FCSTD DOCUMENT  (FreeCAD 0.19R24276 (Git))
Label: Master_sketch_3_1
License: All rights reserved
LicenseURL: http://en.wikipedia.org/wiki/All_rights_reserved
objects: Sketcher::SketchObject×1, PartDesign::Body×1
note: 2 computed .brp shape members not serialized (recipe doc carries the construction recipe); baked Part::Feature solids carry a one-line shape summary decoded from their .brp

FEATURE [Sketcher::SketchObject] Sketch
  FullyConstrained = false
  MapMode = 5
  Support = -> [XY_Plane]
  sketch-geometry (179):
    g0: LineSegment StartX=-41 StartY=82 StartZ=0 EndX=39 EndY=82 EndZ=0
    g1: LineSegment StartX=39 StartY=82 StartZ=0 EndX=39 EndY=71 EndZ=0
    g2: LineSegment StartX=39 StartY=71 StartZ=0 EndX=-41 EndY=71 EndZ=0
    g3: LineSegment StartX=-41 StartY=71 StartZ=0 EndX=-41 EndY=82 EndZ=0
    g4: LineSegment StartX=-26 StartY=82 StartZ=0 EndX=-26 EndY=71 EndZ=0
    g5: LineSegment StartX=24 StartY=82 StartZ=0 EndX=24 EndY=71 EndZ=0
    g6: LineSegment StartX=-41 StartY=71 StartZ=0 EndX=-26 EndY=82 EndZ=0
    g7: LineSegment StartX=-41 StartY=82 StartZ=0 EndX=-26 EndY=71 EndZ=0
    g8: LineSegment StartX=24 StartY=71 StartZ=0 EndX=39 EndY=82 EndZ=0
    g9: LineSegment StartX=24 StartY=82 StartZ=0 EndX=39 EndY=71 EndZ=0
    g10: LineSegment StartX=-41 StartY=108 StartZ=0 EndX=39 EndY=108 EndZ=0
    g11: LineSegment StartX=39 StartY=108 StartZ=0 EndX=39 EndY=119 EndZ=0
    g12: LineSegment StartX=39 StartY=119 StartZ=0 EndX=-41 EndY=119 EndZ=0
    g13: LineSegment StartX=-41 StartY=119 StartZ=0 EndX=-41 EndY=108 EndZ=0
    g14: LineSegment StartX=-26 StartY=108 StartZ=0 EndX=-26 EndY=119 EndZ=0
    g15: LineSegment StartX=24 StartY=108 StartZ=0 EndX=24 EndY=119 EndZ=0
    g16: LineSegment StartX=-41 StartY=119 StartZ=0 EndX=-26 EndY=108 EndZ=0
    g17: LineSegment StartX=-41 StartY=108 StartZ=0 EndX=-26 EndY=119 EndZ=0
    g18: LineSegment StartX=24 StartY=119 StartZ=0 EndX=39 EndY=108 EndZ=0
    g19: LineSegment StartX=24 StartY=108 StartZ=0 EndX=39 EndY=119 EndZ=0
    g20: LineSegment StartX=-41 StartY=153 StartZ=0 EndX=14 EndY=153 EndZ=0
    g21: LineSegment StartX=39 StartY=153 StartZ=0 EndX=39 EndY=142 EndZ=0
    g22: LineSegment StartX=39 StartY=142 StartZ=0 EndX=19 EndY=142 EndZ=0
    g23: LineSegment StartX=-41 StartY=142 StartZ=0 EndX=-41 EndY=153 EndZ=0
    g24: LineSegment StartX=-26 StartY=153 StartZ=0 EndX=-26 EndY=142 EndZ=0
    g25: LineSegment StartX=24 StartY=153 StartZ=0 EndX=24 EndY=142 EndZ=0
    g26: LineSegment StartX=-41 StartY=142 StartZ=0 EndX=-26 EndY=153 EndZ=0
    g27: LineSegment StartX=-41 StartY=153 StartZ=0 EndX=-26 EndY=142 EndZ=0
    g28: LineSegment StartX=24 StartY=142 StartZ=0 EndX=39 EndY=153 EndZ=0
    g29: LineSegment StartX=24 StartY=153 StartZ=0 EndX=39 EndY=142 EndZ=0
    g30: LineSegment StartX=-116.97 StartY=98 StartZ=0 EndX=24 EndY=98 EndZ=0
    g31: LineSegment StartX=24 StartY=98 StartZ=0 EndX=24 EndY=92 EndZ=0
    g32: LineSegment StartX=24 StartY=92 StartZ=0 EndX=-116.97 EndY=92 EndZ=0
    g33: LineSegment StartX=-116.97 StartY=92 StartZ=0 EndX=-116.97 EndY=98 EndZ=0
    g34: LineSegment StartX=-25 StartY=122 StartZ=0 EndX=-12.5 EndY=122 EndZ=0
    g35: LineSegment StartX=23 StartY=122 StartZ=0 EndX=23 EndY=70 EndZ=0
    g36: LineSegment StartX=23 StartY=70 StartZ=0 EndX=-25 EndY=70 EndZ=0
    g37: LineSegment StartX=12.5 StartY=122 StartZ=0 EndX=12.5 EndY=201.661 EndZ=0
    g38: LineSegment StartX=12.5 StartY=201.661 StartZ=0 EndX=-12.5 EndY=201.661 EndZ=0
    g39: LineSegment StartX=-12.5 StartY=201.661 StartZ=0 EndX=-12.5 EndY=122 EndZ=0
    g40: LineSegment StartX=19 StartY=153 StartZ=0 EndX=19 EndY=142 EndZ=0
    g41: LineSegment StartX=14 StartY=131 StartZ=0 EndX=14 EndY=153 EndZ=0
    g42: LineSegment StartX=14 StartY=131 StartZ=0 EndX=43.35 EndY=131 EndZ=0
    g43: LineSegment StartX=60.35 StartY=140 StartZ=0 EndX=24 EndY=140 EndZ=0
    g44: LineSegment StartX=60.35 StartY=140 StartZ=0 EndX=60.35 EndY=10 EndZ=0
    g45: LineSegment StartX=43.35 StartY=70 StartZ=0 EndX=43.35 EndY=102 EndZ=0
    g46: LineSegment StartX=25.35 StartY=70 StartZ=0 EndX=43.35 EndY=70 EndZ=0
    g47: LineSegment StartX=25.35 StartY=107 StartZ=0 EndX=43.35 EndY=107 EndZ=0
    g48: LineSegment StartX=43.35 StartY=102 StartZ=0 EndX=25.35 EndY=102 EndZ=0
    g49: LineSegment StartX=25.35 StartY=102 StartZ=0 EndX=25.35 EndY=107 EndZ=0
    g50: LineSegment StartX=43.35 StartY=107 StartZ=0 EndX=43.35 EndY=131 EndZ=0
    g51: LineSegment StartX=14 StartY=142 StartZ=0 EndX=-41 EndY=142 EndZ=0
    g52: LineSegment StartX=-115.97 StartY=100 StartZ=0 EndX=-99.97 EndY=100 EndZ=0
    g53: LineSegment StartX=-99.97 StartY=100 StartZ=0 EndX=-99.97 EndY=90 EndZ=0
    g54: LineSegment StartX=-99.97 StartY=90 StartZ=0 EndX=-115.97 EndY=90 EndZ=0
    g55: LineSegment StartX=-115.97 StartY=90 StartZ=0 EndX=-115.97 EndY=100 EndZ=0
    g56: LineSegment StartX=-110.97 StartY=90 StartZ=0 EndX=-104.97 EndY=90 EndZ=0
    g57: LineSegment StartX=-104.97 StartY=90 StartZ=0 EndX=-104.97 EndY=80 EndZ=0
    g58: LineSegment StartX=-104.97 StartY=80 StartZ=0 EndX=-110.97 EndY=80 EndZ=0
    g59: LineSegment StartX=-110.97 StartY=80 StartZ=0 EndX=-110.97 EndY=90 EndZ=0
    g60: LineSegment StartX=-123.97 StartY=80 StartZ=0 EndX=-91.97 EndY=80 EndZ=0
    g61: LineSegment StartX=-91.97 StartY=80 StartZ=0 EndX=-91.97 EndY=30 EndZ=0
    g62: LineSegment StartX=-91.97 StartY=30 StartZ=0 EndX=-123.97 EndY=30 EndZ=0
    g63: LineSegment StartX=-123.97 StartY=30 StartZ=0 EndX=-123.97 EndY=80 EndZ=0
    g64: LineSegment StartX=-41 StartY=193.983 StartZ=0 EndX=14 EndY=193.983 EndZ=0
    g65: LineSegment StartX=39 StartY=193.983 StartZ=0 EndX=39 EndY=182.983 EndZ=0
    g66: LineSegment StartX=39 StartY=182.983 StartZ=0 EndX=19 EndY=182.983 EndZ=0
    g67: LineSegment StartX=-41 StartY=182.983 StartZ=0 EndX=-41 EndY=193.983 EndZ=0
    g68: LineSegment StartX=-26 StartY=193.983 StartZ=0 EndX=-26 EndY=182.983 EndZ=0
    g69: LineSegment StartX=24 StartY=193.983 StartZ=0 EndX=24 EndY=182.983 EndZ=0
    g70: LineSegment StartX=-41 StartY=182.983 StartZ=0 EndX=-26 EndY=193.983 EndZ=0
    g71: LineSegment StartX=-41 StartY=193.983 StartZ=0 EndX=-26 EndY=182.983 EndZ=0
    g72: LineSegment StartX=24 StartY=182.983 StartZ=0 EndX=39 EndY=193.983 EndZ=0
    g73: LineSegment StartX=24 StartY=193.983 StartZ=0 EndX=39 EndY=182.983 EndZ=0
    g74: LineSegment StartX=-26 StartY=142 StartZ=0 EndX=55.8269 EndY=142 EndZ=0
    g75: LineSegment StartX=55.8269 StartY=142 StartZ=0 EndX=55.8269 EndY=181.174 EndZ=0
    g76: LineSegment StartX=55.8269 StartY=181.174 StartZ=0 EndX=-36.273 EndY=181.174 EndZ=0
    g77: LineSegment StartX=-26 StartY=156.804 StartZ=0 EndX=-26 EndY=142 EndZ=0
    g78: LineSegment StartX=24 StartY=142 StartZ=0 EndX=-57.8269 EndY=142 EndZ=0
    g79: LineSegment StartX=-57.8269 StartY=142 StartZ=0 EndX=-57.8269 EndY=155.698 EndZ=0
    g80: LineSegment StartX=-57.8269 StartY=155.698 StartZ=0 EndX=34.273 EndY=155.698 EndZ=0
    g81: LineSegment StartX=24 StartY=157.131 StartZ=0 EndX=24 EndY=142 EndZ=0
    g82: LineSegment StartX=64.4469 StartY=144 StartZ=0 EndX=-180 EndY=144 EndZ=0
    g83: LineSegment StartX=-180 StartY=150 StartZ=0 EndX=64.4469 EndY=150 EndZ=0
    g84: LineSegment StartX=64.4469 StartY=150 StartZ=0 EndX=64.4469 EndY=144 EndZ=0
    g85: LineSegment StartX=24 StartY=142 StartZ=0 EndX=24 EndY=140 EndZ=0
    g86: LineSegment StartX=25.35 StartY=70 StartZ=0 EndX=25.35 EndY=10 EndZ=0
    g87: LineSegment StartX=25.35 StartY=10 StartZ=0 EndX=60.35 EndY=10 EndZ=0
    g88: LineSegment StartX=-27.35 StartY=70 StartZ=0 EndX=-62.35 EndY=70 EndZ=0
    g89: LineSegment StartX=-62.35 StartY=70 StartZ=0 EndX=-62.35 EndY=10 EndZ=0
    g90: LineSegment StartX=-62.35 StartY=10 StartZ=0 EndX=-27.35 EndY=10 EndZ=0
    g91: LineSegment StartX=-27.35 StartY=10 StartZ=0 EndX=-27.35 EndY=70 EndZ=0
    g92: LineSegment StartX=60.35 StartY=10 StartZ=0 EndX=-239.65 EndY=10 EndZ=0
    g93: LineSegment StartX=-239.65 StartY=10 StartZ=0 EndX=-239.65 EndY=0 EndZ=0
    g94: LineSegment StartX=-239.65 StartY=0 StartZ=0 EndX=60.35 EndY=0 EndZ=0
    g95: LineSegment StartX=60.35 StartY=0 StartZ=0 EndX=60.35 EndY=10 EndZ=0
    g96: LineSegment StartX=110 StartY=202.513 StartZ=0 EndX=190 EndY=202.513 EndZ=0
    g97: LineSegment StartX=190 StartY=202.513 StartZ=0 EndX=190 EndY=213.513 EndZ=0
    g98: LineSegment StartX=190 StartY=213.513 StartZ=0 EndX=110 EndY=213.513 EndZ=0
    g99: LineSegment StartX=110 StartY=213.513 StartZ=0 EndX=110 EndY=202.513 EndZ=0
    g100: LineSegment StartX=125 StartY=202.513 StartZ=0 EndX=125 EndY=213.513 EndZ=0
    g101: LineSegment StartX=175 StartY=202.513 StartZ=0 EndX=175 EndY=213.513 EndZ=0
    g102: LineSegment StartX=110 StartY=213.513 StartZ=0 EndX=125 EndY=202.513 EndZ=0
    g103: LineSegment StartX=110 StartY=202.513 StartZ=0 EndX=125 EndY=213.513 EndZ=0
    g104: LineSegment StartX=175 StartY=213.513 StartZ=0 EndX=190 EndY=202.513 EndZ=0
    g105: LineSegment StartX=175 StartY=202.513 StartZ=0 EndX=190 EndY=213.513 EndZ=0
    g106: LineSegment StartX=0 StartY=0 StartZ=0 EndX=0 EndY=201.661 EndZ=0
    g107: LineSegment StartX=150 StartY=253.536 StartZ=0 EndX=150 EndY=202.513 EndZ=0
    g108: LineSegment StartX=-36.273 StartY=181.174 StartZ=0 EndX=-36.273 EndY=168.938 EndZ=0
    g109: LineSegment StartX=-36.273 StartY=168.938 StartZ=0 EndX=-26 EndY=168.938 EndZ=0
    g110: LineSegment StartX=-26 StartY=168.938 StartZ=0 EndX=-26 EndY=156.804 EndZ=0
    g111: LineSegment StartX=34.273 StartY=155.698 StartZ=0 EndX=34.273 EndY=168.938 EndZ=0
    g112: LineSegment StartX=34.273 StartY=168.938 StartZ=0 EndX=24 EndY=168.938 EndZ=0
    g113: LineSegment StartX=24 StartY=168.938 StartZ=0 EndX=24 EndY=157.131 EndZ=0
    g114: LineSegment StartX=28.773 StartY=171.908 StartZ=0 EndX=172.865 EndY=171.908 EndZ=0
    g115: LineSegment StartX=172.865 StartY=171.908 StartZ=0 EndX=172.865 EndY=164.124 EndZ=0
    g116: LineSegment StartX=172.865 StartY=164.124 StartZ=0 EndX=28.773 EndY=164.124 EndZ=0
    g117: LineSegment StartX=28.773 StartY=164.124 StartZ=0 EndX=28.773 EndY=171.908 EndZ=0
    g118: LineSegment StartX=128.455 StartY=160.686 StartZ=0 EndX=171.545 EndY=160.686 EndZ=0
    g119: LineSegment StartX=171.545 StartY=253.536 StartZ=0 EndX=128.455 EndY=253.536 EndZ=0
    g120: LineSegment StartX=128.455 StartY=253.536 StartZ=0 EndX=128.455 EndY=160.686 EndZ=0
    g121: LineSegment StartX=-12.5 StartY=201.661 StartZ=0 EndX=204.13 EndY=201.661 EndZ=0
    g122: LineSegment StartX=204.13 StartY=201.661 StartZ=0 EndX=204.13 EndY=214.859 EndZ=0
    g123: LineSegment StartX=204.13 StartY=214.859 StartZ=0 EndX=-12.5 EndY=214.859 EndZ=0
    g124: LineSegment StartX=-12.5 StartY=214.859 StartZ=0 EndX=-12.5 EndY=201.661 EndZ=0
    g125: LineSegment StartX=171.545 StartY=253.536 StartZ=0 EndX=171.545 EndY=160.686 EndZ=0
    g126: LineSegment StartX=-122.448 StartY=228.651 StartZ=0 EndX=-177.552 EndY=228.651 EndZ=0
    g127: LineSegment StartX=-177.552 StartY=228.651 StartZ=0 EndX=-177.552 EndY=239.651 EndZ=0
    g128: LineSegment StartX=-177.552 StartY=239.651 StartZ=0 EndX=-122.448 EndY=239.651 EndZ=0
    g129: LineSegment StartX=-122.448 StartY=239.651 StartZ=0 EndX=-122.448 EndY=228.651 EndZ=0
    g130: LineSegment StartX=-107.448 StartY=228.651 StartZ=0 EndX=-107.448 EndY=239.651 EndZ=0
    g131: LineSegment StartX=-192.552 StartY=228.651 StartZ=0 EndX=-192.552 EndY=239.651 EndZ=0
    g132: LineSegment StartX=-122.448 StartY=239.651 StartZ=0 EndX=-107.448 EndY=228.651 EndZ=0
    g133: LineSegment StartX=-122.448 StartY=228.651 StartZ=0 EndX=-107.448 EndY=239.651 EndZ=0
    g134: LineSegment StartX=-192.552 StartY=239.651 StartZ=0 EndX=-177.552 EndY=228.651 EndZ=0
    g135: LineSegment StartX=-192.552 StartY=228.651 StartZ=0 EndX=-177.552 EndY=239.651 EndZ=0
    g136: LineSegment StartX=-126.618 StartY=244.672 StartZ=0 EndX=12.5 EndY=244.672 EndZ=0
    g137: LineSegment StartX=12.5 StartY=244.672 StartZ=0 EndX=12.5 EndY=222.99 EndZ=0
    g138: LineSegment StartX=12.5 StartY=222.99 StartZ=0 EndX=-126.618 EndY=222.99 EndZ=0
    g139: LineSegment StartX=-126.618 StartY=222.99 StartZ=0 EndX=-126.618 EndY=244.672 EndZ=0
    g140: LineSegment StartX=12.5 StartY=201.661 StartZ=0 EndX=-12.5 EndY=201.661 EndZ=0
    g141: LineSegment StartX=-12.5 StartY=201.661 StartZ=0 EndX=-12.5 EndY=249.397 EndZ=0
    g142: LineSegment StartX=-12.5 StartY=249.397 StartZ=0 EndX=12.5 EndY=249.397 EndZ=0
    g143: LineSegment StartX=12.5 StartY=249.397 StartZ=0 EndX=12.5 EndY=201.661 EndZ=0
    g144: LineSegment StartX=-168.275 StartY=254.074 StartZ=0 EndX=-131.725 EndY=254.074 EndZ=0
    g145: LineSegment StartX=-131.725 StartY=254.074 StartZ=0 EndX=-131.725 EndY=176.029 EndZ=0
    g146: LineSegment StartX=-131.725 StartY=176.029 StartZ=0 EndX=-168.275 EndY=176.029 EndZ=0
    g147: LineSegment StartX=-168.275 StartY=176.029 StartZ=0 EndX=-168.275 EndY=254.074 EndZ=0
    g148: LineSegment StartX=-150 StartY=228.651 StartZ=0 EndX=-150 EndY=254.074 EndZ=0
    g149: LineSegment StartX=19 StartY=153 StartZ=0 EndX=19 EndY=176.767 EndZ=0
    g150: LineSegment StartX=19 StartY=196.705 StartZ=0 EndX=14 EndY=196.705 EndZ=0
    g151: LineSegment StartX=14 StartY=196.705 StartZ=0 EndX=14 EndY=153 EndZ=0
    g152: LineSegment StartX=19 StartY=153 StartZ=0 EndX=39 EndY=153 EndZ=0
    g153: LineSegment StartX=14 StartY=182.983 StartZ=0 EndX=-41 EndY=182.983 EndZ=0
    g154: LineSegment StartX=19 StartY=193.983 StartZ=0 EndX=39 EndY=193.983 EndZ=0
    g155: LineSegment StartX=19 StartY=182.983 StartZ=0 EndX=24 EndY=182.983 EndZ=0
    g156: LineSegment StartX=24 StartY=182.983 StartZ=0 EndX=24 EndY=168.938 EndZ=0
    g157: LineSegment StartX=19 StartY=182.983 StartZ=0 EndX=19 EndY=196.705 EndZ=0
    g158: LineSegment StartX=19 StartY=176.767 StartZ=0 EndX=17 EndY=176.767 EndZ=0
    g159: LineSegment StartX=17 StartY=176.767 StartZ=0 EndX=17 EndY=196.705 EndZ=0
    g160: LineSegment StartX=-107.97 StartY=80 StartZ=0 EndX=-107.97 EndY=30 EndZ=0
    g161: LineSegment StartX=-107.97 StartY=80 StartZ=0 EndX=-107.97 EndY=90 EndZ=0
    g162: LineSegment StartX=-178 StartY=152 StartZ=0 EndX=-162 EndY=152 EndZ=0
    g163: LineSegment StartX=-162 StartY=152 StartZ=0 EndX=-162 EndY=142 EndZ=0
    g164: LineSegment StartX=-162 StartY=142 StartZ=0 EndX=-178 EndY=142 EndZ=0
    g165: LineSegment StartX=-178 StartY=142 StartZ=0 EndX=-178 EndY=152 EndZ=0
    g166: LineSegment StartX=-173 StartY=142 StartZ=0 EndX=-167 EndY=142 EndZ=0
    g167: LineSegment StartX=-167 StartY=142 StartZ=0 EndX=-167 EndY=132 EndZ=0
    g168: LineSegment StartX=-167 StartY=132 StartZ=0 EndX=-173 EndY=132 EndZ=0
    g169: LineSegment StartX=-173 StartY=132 StartZ=0 EndX=-173 EndY=142 EndZ=0
    g170: LineSegment StartX=-186 StartY=132 StartZ=0 EndX=-154 EndY=132 EndZ=0
    g171: LineSegment StartX=-154 StartY=132 StartZ=0 EndX=-154 EndY=82 EndZ=0
    g172: LineSegment StartX=-154 StartY=82 StartZ=0 EndX=-186 EndY=82 EndZ=0
    g173: LineSegment StartX=-186 StartY=82 StartZ=0 EndX=-186 EndY=132 EndZ=0
    g174: LineSegment StartX=-170 StartY=132 StartZ=0 EndX=-170 EndY=82 EndZ=0
    g175: LineSegment StartX=-170 StartY=111.828 StartZ=0 EndX=-170 EndY=142 EndZ=0
    g176: LineSegment StartX=-180 StartY=144 StartZ=0 EndX=-180 EndY=150 EndZ=0
    g177: LineSegment StartX=-25 StartY=70 StartZ=0 EndX=-25 EndY=122 EndZ=0
    g178: LineSegment StartX=12.5 StartY=122 StartZ=0 EndX=23 EndY=122 EndZ=0
  constraints (481):
    c: Coincident(g0,g1)
    c: Coincident(g1,g2)
    c: Coincident(g2,g3)
    c: Coincident(g3,g0)
    c: Horizontal(g0)
    c: Horizontal(g2)
    c: Vertical(g1)
    c: Vertical(g3)
    c: PointOnObject(g4,g0)
    c: PointOnObject(g4,g2)
    c: Vertical(g4)
    c: PointOnObject(g5,g0)
    c: Vertical(g5)
    c: DistanceX(g2,g2) = 80
    c: DistanceX(g4,g5) = 50
    c: DistanceY(g3,g3) = 11
    c: Coincident(g6,g2)
    c: Coincident(g6,g4)
    c: Coincident(g7,g0)
    c: Coincident(g7,g4)
    c: Coincident(g8,g5)
    c: Coincident(g8,g0)
    c: Coincident(g9,g5)
    c: Coincident(g9,g1)
    c: DistanceX(g2,g4) = 15
    c: Coincident(g10,g11)
    c: Coincident(g11,g12)
    c: Coincident(g12,g13)
    c: Coincident(g13,g10)
    c: Horizontal(g10)
    c: Horizontal(g12)
    c: Vertical(g11)
    c: Vertical(g13)
    c: PointOnObject(g14,g10)
    c: PointOnObject(g14,g12)
    c: Vertical(g14)
    c: PointOnObject(g15,g10)
    c: Vertical(g15)
    c: Coincident(g16,g12)
    c: Coincident(g16,g14)
    c: Coincident(g17,g10)
    c: Coincident(g17,g14)
    c: Coincident(g18,g15)
    c: Coincident(g18,g10)
    c: Coincident(g19,g15)
    c: Coincident(g19,g11)
    c: Coincident(g152,g21)
    c: Coincident(g21,g22)
    c: Coincident(g51,g23)
    c: Coincident(g23,g20)
    c: Horizontal(g20)
    c: Horizontal(g22)
    c: Vertical(g21)
    c: Vertical(g23)
    c: PointOnObject(g24,g20)
    c: PointOnObject(g24,g22)
    c: Vertical(g24)
    c: PointOnObject(g25,g20)
    c: Vertical(g25)
    c: Coincident(g26,g51)
    c: Coincident(g26,g24)
    c: Coincident(g27,g20)
    c: Coincident(g27,g24)
    c: Coincident(g28,g25)
    c: Coincident(g28,g152)
    c: Coincident(g29,g25)
    c: Coincident(g29,g21)
    c: Equal(g10,g2)
    c: Equal(g1,g11)
    c: Equal(g15,g11)
    c: Equal(g16,g7)
    c: Equal(g19,g8)
    c: Horizontal(g5,g1)
    c: Horizontal(g25,g21)
    c: Equal(g21,g11)
    c: Equal(g18,g29)
    c: Equal(g27,g16)
    c: Vertical(g4,g14)
    c: Vertical(g14,g24)
    c: Coincident(g30,g31)
    c: Coincident(g31,g32)
    c: Coincident(g32,g33)
    c: Coincident(g33,g30)
    c: Horizontal(g30)
    c: Horizontal(g32)
    c: Vertical(g31)
    c: Vertical(g33)
    c: Coincident(g178,g35)
    c: Coincident(g35,g36)
    c: Horizontal(g34)
    c: Horizontal(g36)
    c: Vertical(g35)
    c: DistanceX(g4,g36) = 1
    c: Coincident(g37,g38)
    c: Coincident(g38,g39)
    c: Horizontal(g38)
    c: Vertical(g37)
    c: Vertical(g39)
    c: DistanceX(g38,g37) = 25
    c: DistanceX(g34,g39) = 12.5
    c: Vertical(g40)
    c: Vertical(g41)
    c: Horizontal(g42)
    c: Horizontal(g43)
    c: Vertical(g44)
    c: Vertical(g45)
    c: Horizontal(g46)
    c: Coincident(g48,g49)
    c: Coincident(g49,g47)
    c: Horizontal(g47)
    c: Horizontal(g48)
    c: Vertical(g49)
    c: Tangent(g45,g50)
    c: Vertical(g46,g48)
    c: PointOnObject(g51,g41)
    c: Tangent(g22,g51)
    c: Coincident(g43,g44)
    c: Coincident(g46,g45)
    c: Coincident(g45,g48)
    c: Coincident(g47,g50)
    c: Coincident(g52,g53)
    c: Coincident(g53,g54)
    c: Coincident(g54,g55)
    c: Coincident(g55,g52)
    c: Horizontal(g52)
    c: Horizontal(g54)
    c: Vertical(g53)
    c: Vertical(g55)
    c: Coincident(g56,g57)
    c: Coincident(g57,g58)
    c: Coincident(g58,g59)
    c: Coincident(g59,g56)
    c: Horizontal(g56)
    c: Horizontal(g58)
    c: Vertical(g57)
    c: Vertical(g59)
    c: PointOnObject(g56,g54)
    c: Coincident(g60,g61)
    c: Coincident(g61,g62)
    c: Coincident(g62,g63)
    c: Coincident(g63,g60)
    c: Horizontal(g60)
    c: Horizontal(g62)
    c: Vertical(g61)
    c: Vertical(g63)
    c: Coincident(g154,g65)
    c: Coincident(g65,g66)
    c: Coincident(g153,g67)
    c: Coincident(g67,g64)
    c: Horizontal(g64)
    c: Horizontal(g66)
    c: Vertical(g65)
    c: Vertical(g67)
    c: PointOnObject(g68,g64)
    c: PointOnObject(g68,g66)
    c: Vertical(g68)
    c: PointOnObject(g69,g64)
    c: Vertical(g69)
    c: Coincident(g70,g153)
    c: Coincident(g70,g68)
    c: Coincident(g71,g64)
    c: Coincident(g71,g68)
    c: Coincident(g72,g69)
    c: Coincident(g72,g154)
    c: Coincident(g73,g69)
    c: Coincident(g73,g65)
    c: Equal(g69,g65)
    c: Equal(g65,g21)
    c: Equal(g73,g29)
    c: Equal(g71,g27)
    c: Vertical(g153,g0)
    c: DistanceX(g5,g46) = 1.35
    c: DistanceX(g46,g46) = 18
    c: DistanceY(g45,g1) = 1
    c: DistanceY(g47,g10) = 1
    c: DistanceY(g43,g21) = 2
    c: DistanceX(g40,g25) = 5
    c: Coincident(g42,g50)
    c: DistanceX(g35,g31) = 1
    c: DistanceX(g32,g54) = 1
    c: Coincident(g74,g75)
    c: Coincident(g75,g76)
    c: Coincident(g77,g74)
    c: Horizontal(g74)
    c: Horizontal(g76)
    c: Vertical(g75)
    c: Vertical(g77)
    c: Coincident(g74,g24)
    c: Coincident(g78,g79)
    c: Coincident(g79,g80)
    c: Coincident(g81,g78)
    c: Horizontal(g78)
    c: Horizontal(g80)
    c: Vertical(g79)
    c: Vertical(g81)
    c: Coincident(g78,g25)
    c: Coincident(g41,g42)
    c: Coincident(g83,g84)
    c: Coincident(g84,g82)
    c: Horizontal(g82)
    c: Horizontal(g83)
    c: Vertical(g84)
    c: Coincident(g85,g25)
    c: Vertical(g85)
    c: Coincident(g43,g85)
    c: Coincident(g40,g22)
    c: Coincident(g86,g87)
    c: Horizontal(g87)
    c: Vertical(g86)
    c: Coincident(g88,g89)
    c: Coincident(g89,g90)
    c: Coincident(g90,g91)
    c: Coincident(g91,g88)
    c: Horizontal(g88)
    c: Horizontal(g90)
    c: Vertical(g89)
    c: Vertical(g91)
    c: Horizontal(g90,g86)
    c: Equal(g90,g87)
    c: Coincident(g92,g93)
    c: Coincident(g93,g94)
    c: Coincident(g94,g95)
    c: Coincident(g95,g92)
    c: Horizontal(g92)
    c: Horizontal(g94)
    c: Vertical(g93)
    c: Vertical(g95)
    c: Coincident(g92,g87)
    c: Coincident(g96,g97)
    c: Coincident(g97,g98)
    c: Coincident(g98,g99)
    c: Coincident(g99,g96)
    c: Horizontal(g96)
    c: Vertical(g97)
    c: Vertical(g99)
    c: PointOnObject(g100,g96)
    c: PointOnObject(g100,g98)
    c: Vertical(g100)
    c: PointOnObject(g101,g96)
    c: Vertical(g101)
    c: Coincident(g102,g98)
    c: Coincident(g102,g100)
    c: Coincident(g103,g96)
    c: Coincident(g103,g100)
    c: Coincident(g104,g101)
    c: Coincident(g104,g96)
    c: Coincident(g105,g101)
    c: Coincident(g105,g97)
    c: Equal(g101,g97)
    c: Equal(g97,g65)
    c: Equal(g65,g99)
    c: Parallel(g105,g72)
    c: Parallel(g102,g71)
    c: Vertical(g106)
    c: Symmetric(g38,g37,g106)
    c: Vertical(g107)
    c: Symmetric(g96,g96,g107)
    c: DistanceX(g106,g107) = 150
    c: Coincident(g108,g109)
    c: Coincident(g109,g110)
    c: Horizontal(g109)
    c: Vertical(g108)
    c: Vertical(g110)
    c: Coincident(g111,g112)
    c: Coincident(g112,g113)
    c: Horizontal(g112)
    c: Vertical(g111)
    c: Vertical(g113)
    c: Horizontal(g109,g112)
    c: Equal(g109,g112)
    c: Coincident(g77,g110)
    c: Coincident(g108,g76)
    c: Coincident(g111,g80)
    c: Coincident(g81,g113)
    c: Equal(g78,g74)
    c: DistanceX(g41,g40) = 5
    c: DistanceX(g88,g4) = 1.35
    c: DistanceX(g75,g83) = 8.62
    c: Coincident(g114,g115)
    c: Coincident(g115,g116)
    c: Coincident(g116,g117)
    c: Coincident(g117,g114)
    c: Horizontal(g114)
    c: Horizontal(g116)
    c: Vertical(g115)
    c: Vertical(g117)
    c: Coincident(g119,g120)
    c: Coincident(g120,g118)
    c: Horizontal(g118)
    c: Horizontal(g119)
    c: Vertical(g120)
    c: Coincident(g121,g122)
    c: Coincident(g122,g123)
    c: Coincident(g123,g124)
    c: Coincident(g124,g121)
    c: Horizontal(g121)
    c: Horizontal(g123)
    c: Vertical(g122)
    c: Vertical(g124)
    c: Coincident(g121,g38)
    c: Vertical(g125)
    c: Coincident(g125,g118)
    c: Coincident(g119,g125)
    c: Horizontal(g88,g46)
    c: Coincident(g126,g127)
    c: Coincident(g127,g128)
    c: Coincident(g128,g129)
    c: Coincident(g129,g126)
    c: Horizontal(g126)
    c: Horizontal(g128)
    c: Vertical(g127)
    c: Vertical(g129)
    c: PointOnObject(g130,g126)
    c: PointOnObject(g130,g128)
    c: Vertical(g130)
    c: PointOnObject(g131,g126)
    c: Vertical(g131)
    c: Coincident(g132,g128)
    c: Coincident(g132,g130)
    c: Coincident(g133,g126)
    c: Coincident(g133,g130)
    c: Coincident(g134,g131)
    c: Coincident(g134,g126)
    c: Coincident(g135,g131)
    c: Coincident(g135,g127)
    c: Equal(g131,g127)
    c: Equal(g127,g65)
    c: Parallel(g135,g72)
    c: Parallel(g133,g70)
    c: Coincident(g136,g137)
    c: Coincident(g137,g138)
    c: Coincident(g138,g139)
    c: Coincident(g139,g136)
    c: Horizontal(g136)
    c: Horizontal(g138)
    c: Vertical(g137)
    c: Vertical(g139)
    c: Coincident(g140,g141)
    c: Coincident(g141,g142)
    c: Coincident(g142,g143)
    c: Coincident(g143,g140)
    c: Horizontal(g140)
    c: Horizontal(g142)
    c: Vertical(g141)
    c: Vertical(g143)
    c: Coincident(g140,g37)
    c: Vertical(g136,g142)
    c: Vertical(g140,g38)
    c: Coincident(g144,g145)
    c: Coincident(g145,g146)
    c: Coincident(g146,g147)
    c: Coincident(g147,g144)
    c: Horizontal(g144)
    c: Horizontal(g146)
    c: Vertical(g145)
    c: Vertical(g147)
    c: Vertical(g148)
    c: Symmetric(g126,g126,g148)
    c: Symmetric(g144,g144,g148)
    c: DistanceX(g148,g106) = 150
    c: Symmetric(g119,g119,g107)
    c: Coincident(g157,g150)
    c: Coincident(g150,g151)
    c: Horizontal(g150)
    c: Vertical(g149)
    c: Vertical(g151)
    c: Coincident(g20,g41)
    c: Coincident(g152,g40)
    c: Tangent(g20,g152)
    c: PointOnObject(g153,g151)
    c: Tangent(g66,g153)
    c: PointOnObject(g64,g151)
    c: PointOnObject(g154,g149)
    c: Tangent(g64,g154)
    c: Coincident(g155,g156)
    c: Vertical(g156)
    c: Coincident(g155,g66)
    c: Coincident(g69,g155)
    c: Coincident(g157,g66)
    c: Tangent(g149,g157)
    c: Coincident(g158,g159)
    c: Horizontal(g158)
    c: Vertical(g159)
    c: Coincident(g158,g149)
    c: PointOnObject(g159,g150)
    c: DistanceX(g159,g150) = 2
    c: Vertical(g160)
    c: Symmetric(g62,g61,g160)
    c: Symmetric(g58,g57,g160)
    c: DistanceX(g62,g62) = 32
    c: Coincident(g161,g160)
    c: Vertical(g161)
    c: Symmetric(g54,g53,g161)
    c: DistanceX(g160,g106) = 107.97
    c: DistanceX(g94,g94) = 300
    c: DistanceX(g23,g21) = 80
    c: Coincident(g151,g20)
    c: Coincident(g149,g40)
    c: DistanceX(g116,g80) = 5.5
    c: DistanceX(g118,g115) = 1.32
    c: DistanceX(g118,g118) = 43.09
    c: DistanceX(g146,g146) = 36.55
    c: DistanceX(g97,g122) = 14.13
    c: DistanceX(g138,g126) = 4.17
    c: Coincident(g156,g112)
    c: Coincident(g106,g-1)
    c: DistanceX(g98,g98) = 80
    c: Horizontal(g94,g-1)
    c: DistanceY(g95,g95) = 10
    c: DistanceY(g89,g89) = 60
    c: Coincident(g86,g46)
    c: DistanceX(g89,g90) = 35
    c: DistanceY(g63,g63) = 50
    c: DistanceY(g-1,g160) = 30
    c: Horizontal(g58,g60)
    c: DistanceX(g58,g57) = 6
    c: DistanceX(g54,g54) = 16
    c: DistanceY(g60,g54) = 10
    c: DistanceY(g55,g55) = 10
    c: DistanceY(g33,g33) = 6
    c: Coincident(g162,g163)
    c: Coincident(g163,g164)
    c: Coincident(g164,g165)
    c: Coincident(g165,g162)
    c: Horizontal(g162)
    c: Horizontal(g164)
    c: Vertical(g163)
    c: Vertical(g165)
    c: Coincident(g166,g167)
    c: Coincident(g167,g168)
    c: Coincident(g168,g169)
    c: Coincident(g169,g166)
    c: Horizontal(g166)
    c: Horizontal(g168)
    c: Vertical(g167)
    c: Vertical(g169)
    c: PointOnObject(g166,g164)
    c: Coincident(g170,g171)
    c: Coincident(g171,g172)
    c: Coincident(g172,g173)
    c: Coincident(g173,g170)
    c: Horizontal(g170)
    c: Horizontal(g172)
    c: Vertical(g171)
    c: Vertical(g173)
    c: Vertical(g174)
    c: Symmetric(g172,g171,g174)
    c: Symmetric(g168,g167,g174)
    c: Equal(g62,g172) = 32
    c: Vertical(g175)
    c: Symmetric(g164,g163,g175)
    c: Equal(g63,g173) = 50
    c: Horizontal(g168,g170)
    c: DistanceX(g168,g167) = 6
    c: Equal(g54,g164) = 16
    c: DistanceY(g170,g164) = 10
    c: Equal(g55,g165) = 10
    c: Vertical(g175,g174)
    c: Coincident(g176,g82)
    c: Coincident(g176,g83)
    c: Vertical(g176)
    c: DistanceY(g176,g176) = 6
    c: DistanceY(g164,g82) = 2
    c: DistanceX(g174,g-1) = 170
    c: DistanceX(g83,g162) = 2
    c: DistanceY(g-1,g174) = 82
    c: Coincident(g87,g44)
    c: DistanceY(g44,g44) = 130
    c: DistanceY(g45,g45) = 32
    c: DistanceY(g50,g50) = 24
    c: DistanceY(g49,g49) = 5
    c: DistanceX(g36,g36) = 48
    c: DistanceY(g35,g35) = 52
    c: Horizontal(g35,g46)
    c: Coincident(g177,g36)
    c: Coincident(g177,g34)
    c: Vertical(g177)
    c: DistanceY(g54,g32) = 2
    c: Tangent(g34,g178)
    c: Coincident(g34,g39)
    c: Horizontal(g37,g34)
FEATURE [PartDesign::Body] Body
  Group = -> [Sketch]
  Origin = -> Origin
